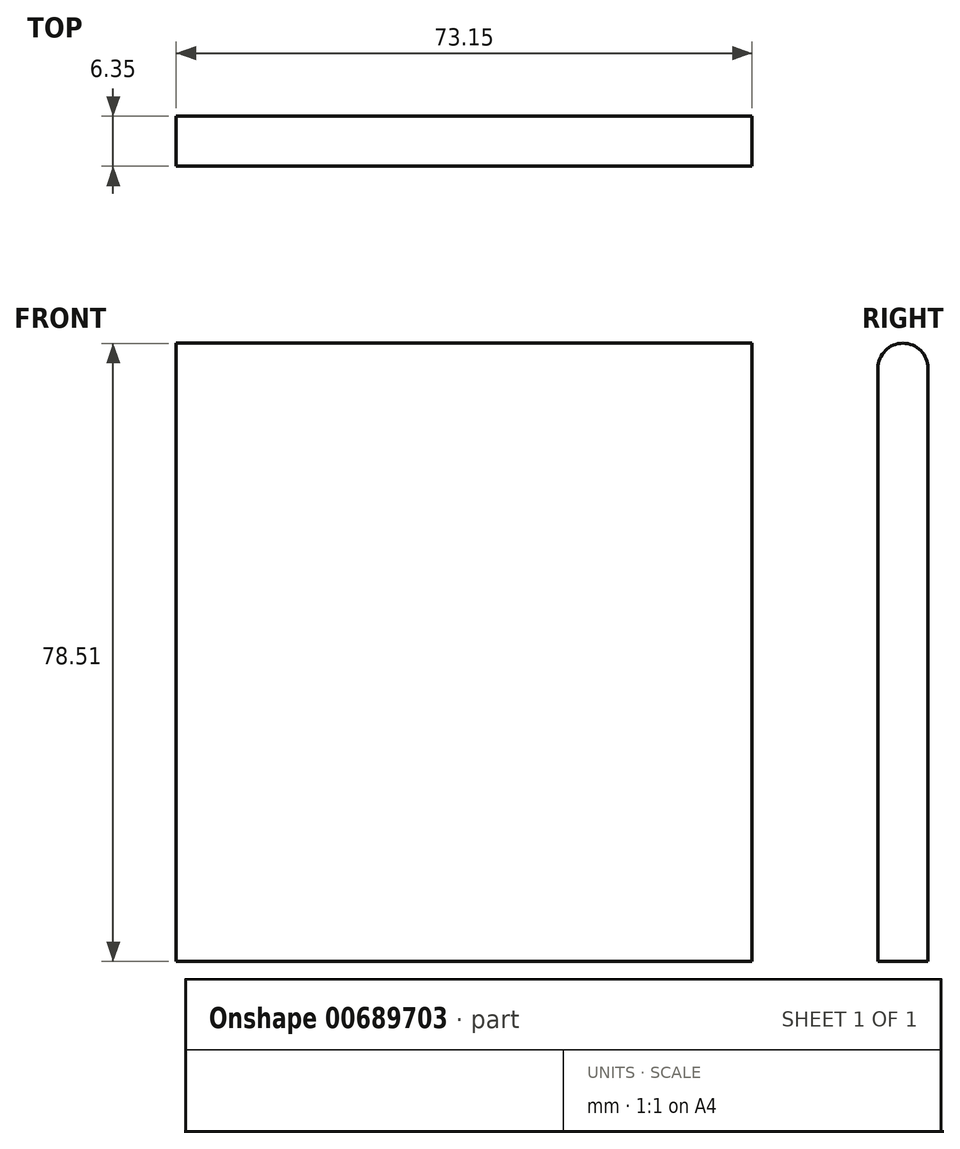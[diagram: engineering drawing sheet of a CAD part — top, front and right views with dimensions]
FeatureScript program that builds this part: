
annotation { "Feature Type Name" : "Feature", "Feature Type Description" : "" }
export const myFeature = defineFeature(function(context is Context, id is Id, definition is map)
    precondition{}
    {
        {
            var Q0;
            Q0=qCreatedBy(makeId("Front.planeOp"),FACE);
            var sketch = newSketch(context, id + "F0", { "sketchPlane" : qUnion([Q0])});
            skLineSegment(sketch, "E0.bottom", {"start": v(36.57, 37.67) * mm, "end": v(-36.57, 37.67) * mm});
            skLineSegment(sketch, "E0.top", {"start": v(36.57, -37.67) * mm, "end": v(-36.57, -37.67) * mm});
            skLineSegment(sketch, "E0.left", {"start": v(36.57, 37.67) * mm, "end": v(36.57, -37.67) * mm});
            skLineSegment(sketch, "E0.right", {"start": v(-36.57, 37.67) * mm, "end": v(-36.57, -37.67) * mm});
            skPoint(sketch, "E0.middle", {"position": v(0, 0) * mm});
            skSolve(sketch);
        }
        {
            var Q0;
            Q0=makeQuery(id+"F0.imprint","IMPRINT",FACE,{"disambiguationData":[TD([[makeQuery(id+"F0.imprint","IMPRINT",EDGE,{"derivedFrom":sQuery(id+"F0.wireOp",EDGE,"E0.bottom")}),1.0]])]});
            extrude(context, id + "F1", {"entities" : qUnion([Q0]), "depth" : 6.35 * mm, "offsetDistance" : 25.4 * mm});
        }
        {
            var Q0;
            Q0=makeQuery(id+"F1.opExtrude","SWEPT_FACE",FACE,{"disambiguationData":[OSD([sQuery(id+"F0.wireOp",EDGE,"E0.right")])]});
            var sketch = newSketch(context, id + "F2", { "sketchPlane" : qUnion([Q0])});
            skArc(sketch, "E1", {"start": v(6.35, 37.67) * mm, "mid": v(3.18, 40.84) * mm, "end": v(0, 37.67) * mm});
            skSolve(sketch);
        }
        {
            var Q0;
            Q0=makeQuery(id+"F2.imprint","IMPRINT",FACE,{"disambiguationData":[TD([[makeQuery(id+"F2.imprint","IMPRINT",EDGE,{"derivedFrom":sQuery(id+"F2.wireOp",EDGE,"E1")}),1.0]])]});
            extrude(context, id + "F3", {"entities" : qUnion([Q0]), "operationType" : NewBodyOperationType.ADD, "oppositeDirection" : true, "depth" : 73.15 * mm, "offsetDistance" : 25.4 * mm});
        }
        {
            var Q0;
            Q0=makeQuery(id+"F3.opExtrude","CAP_FACE",FACE,{"disambiguationData":[OSD([sQuery(id+"F0.wireOp",EDGE,"E0.bottom"),sQuery(id+"F0.wireOp",EDGE,"E0.right"),sQuery(id+"F2.wireOp",EDGE,"E1")])],"isStart":false});
            var sketch = newSketch(context, id + "F4", { "sketchPlane" : qUnion([Q0])});
            skArc(sketch, "E2", {"start": v(-0.7, 37.67) * mm, "mid": v(-3.2, 40.11) * mm, "end": v(-5.68, 37.67) * mm});
            skSolve(sketch);
        }
        {
            var Q0;
            Q0=sQuery(id+"F4.wireOp",EDGE,"E2");
            extrude(context, id + "F5", {"bodyType" : ToolBodyType.SURFACE, "surfaceEntities" : qUnion([Q0]), "depth" : -73.15 * mm, "offsetDistance" : 25.4 * mm});
        }
    });
